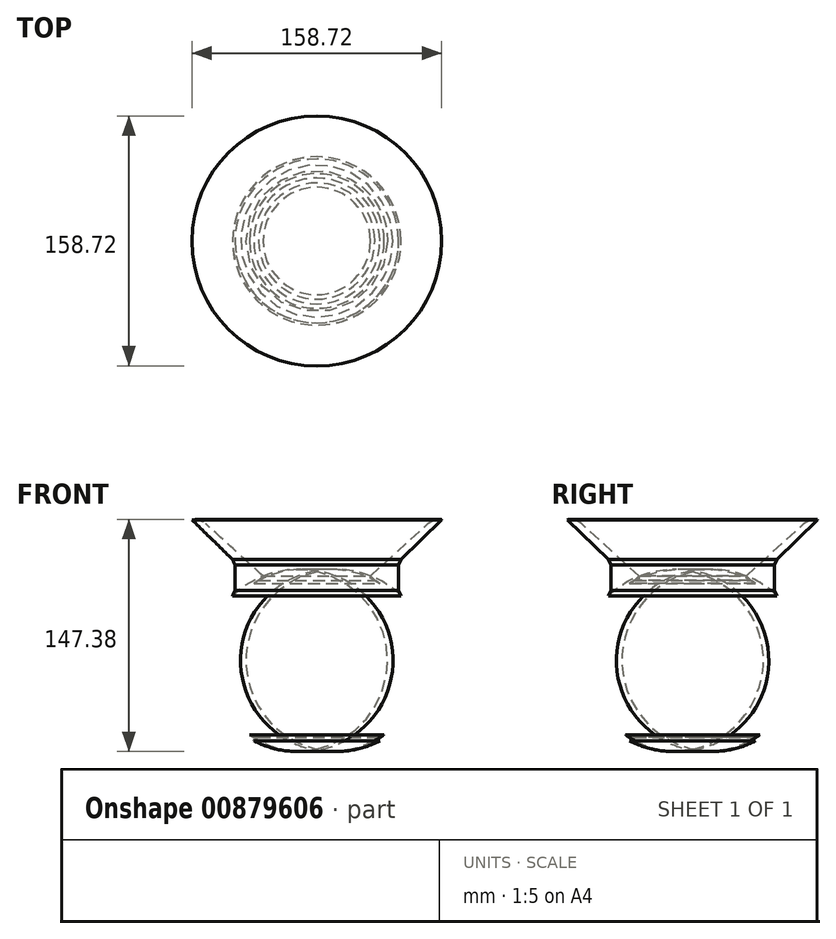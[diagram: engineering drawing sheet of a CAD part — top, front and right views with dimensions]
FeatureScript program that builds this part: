
annotation { "Feature Type Name" : "Feature", "Feature Type Description" : "" }
export const myFeature = defineFeature(function(context is Context, id is Id, definition is map)
    precondition{}
    {
        {
            var Q0;
            Q0=qCreatedBy(makeId("Front.planeOp"),FACE);
            var sketch = newSketch(context, id + "F0", { "sketchPlane" : qUnion([Q0])});
            skLineSegment(sketch, "E0.bottom", {"start": v(0, 0) * mm, "end": v(40, 0) * mm});
            skLineSegment(sketch, "E0.top", {"start": v(0, 2) * mm, "end": v(40, 2) * mm});
            skLineSegment(sketch, "E0.left", {"start": v(0, 0) * mm, "end": v(0, 2) * mm});
            skLineSegment(sketch, "E1", {"start": v(40, 2) * mm, "end": v(40, 102) * mm, "construction": true});
            skArc(sketch, "E2", {"start": v(40, 0) * mm, "mid": v(70.16, 43.65) * mm, "end": v(51.99, 93.5) * mm});
            skLineSegment(sketch, "E3", {"start": v(40, 102) * mm, "end": v(40, 100) * mm, "construction": true});
            skArc(sketch, "E4", {"start": v(40, 2) * mm, "mid": v(67.16, 51) * mm, "end": v(40, 100) * mm});
            skLineSegment(sketch, "E5", {"start": v(51.99, 113.7) * mm, "end": v(79.36, 140.42) * mm});
            skLineSegment(sketch, "E6", {"start": v(79.36, 140.42) * mm, "end": v(77.96, 141.85) * mm});
            skLineSegment(sketch, "E7", {"start": v(36.9, 101.78) * mm, "end": v(40, 100) * mm});
            skLineSegment(sketch, "E8", {"start": v(51.99, 113.7) * mm, "end": v(51.99, 93.5) * mm});
            skLineSegment(sketch, "E9", {"start": v(77.96, 141.85) * mm, "end": v(76.56, 143.28) * mm});
            skLineSegment(sketch, "E10", {"start": v(36.9, 101.78) * mm, "end": v(34.11, 104.64) * mm});
            skLineSegment(sketch, "E11", {"start": v(34.11, 104.64) * mm, "end": v(76.56, 143.28) * mm});
            skSolve(sketch);
        }
        {
            var Q0;
            Q0=makeQuery(id+"F0.imprint","IMPRINT",FACE,{"disambiguationData":[TD([[makeQuery(id+"F0.imprint","IMPRINT",EDGE,{"derivedFrom":sQuery(id+"F0.wireOp",EDGE,"E0.bottom")}),1.0]])]});
            var Q1;
            Q1=sQuery(id+"F0.wireOp",EDGE,"E0.left");
            revolve(context, id + "F1", {"surfaceOperationType" : NewSurfaceOperationType.NEW, "entities" : qUnion([Q0]), "axis" : qUnion([Q1]), "revolveType" : RevolveType.FULL});
        }
        {
            var Q0;
            Q0=makeQuery(id+"F1.opRevolve","SWEPT_EDGE",EDGE,{"disambiguationData":[OSD([sQuery(id+"F0.wireOp",EDGE,"E2"),sQuery(id+"F0.wireOp",EDGE,"E8")])]});
            var Q1;
            Q1=makeQuery(id+"F1.opRevolve","SWEPT_EDGE",EDGE,{"disambiguationData":[OSD([sQuery(id+"F0.wireOp",EDGE,"E5"),sQuery(id+"F0.wireOp",EDGE,"E8")])]});
            chamfer(context, id + "F2", {"entities" : qUnion([Q0, Q1]), "width" : 5 * mm, "tangentPropagation" : true});
        }
        {
            var Q0;
            Q0=makeQuery(id+"F1.opRevolve","SWEPT_EDGE",EDGE,{"disambiguationData":[OSD([sQuery(id+"F0.wireOp",EDGE,"E0.top"),sQuery(id+"F0.wireOp",EDGE,"E4")])]});
            fillet(context, id + "F3", {"entities" : qUnion([Q0]), "radius" : 10 * mm, "tangentPropagation" : true, "allowEdgeOverflow" : false});
        }
        {
            var Q0;
            Q0=makeQuery(id+"F1.opRevolve","SWEPT_EDGE",EDGE,{"disambiguationData":[OSD([sQuery(id+"F0.wireOp",EDGE,"E9"),sQuery(id+"F0.wireOp",EDGE,"E11")])]});
            fillet(context, id + "F4", {"entities" : qUnion([Q0]), "radius" : 10 * mm, "tangentPropagation" : true, "allowEdgeOverflow" : false});
        }
    });
